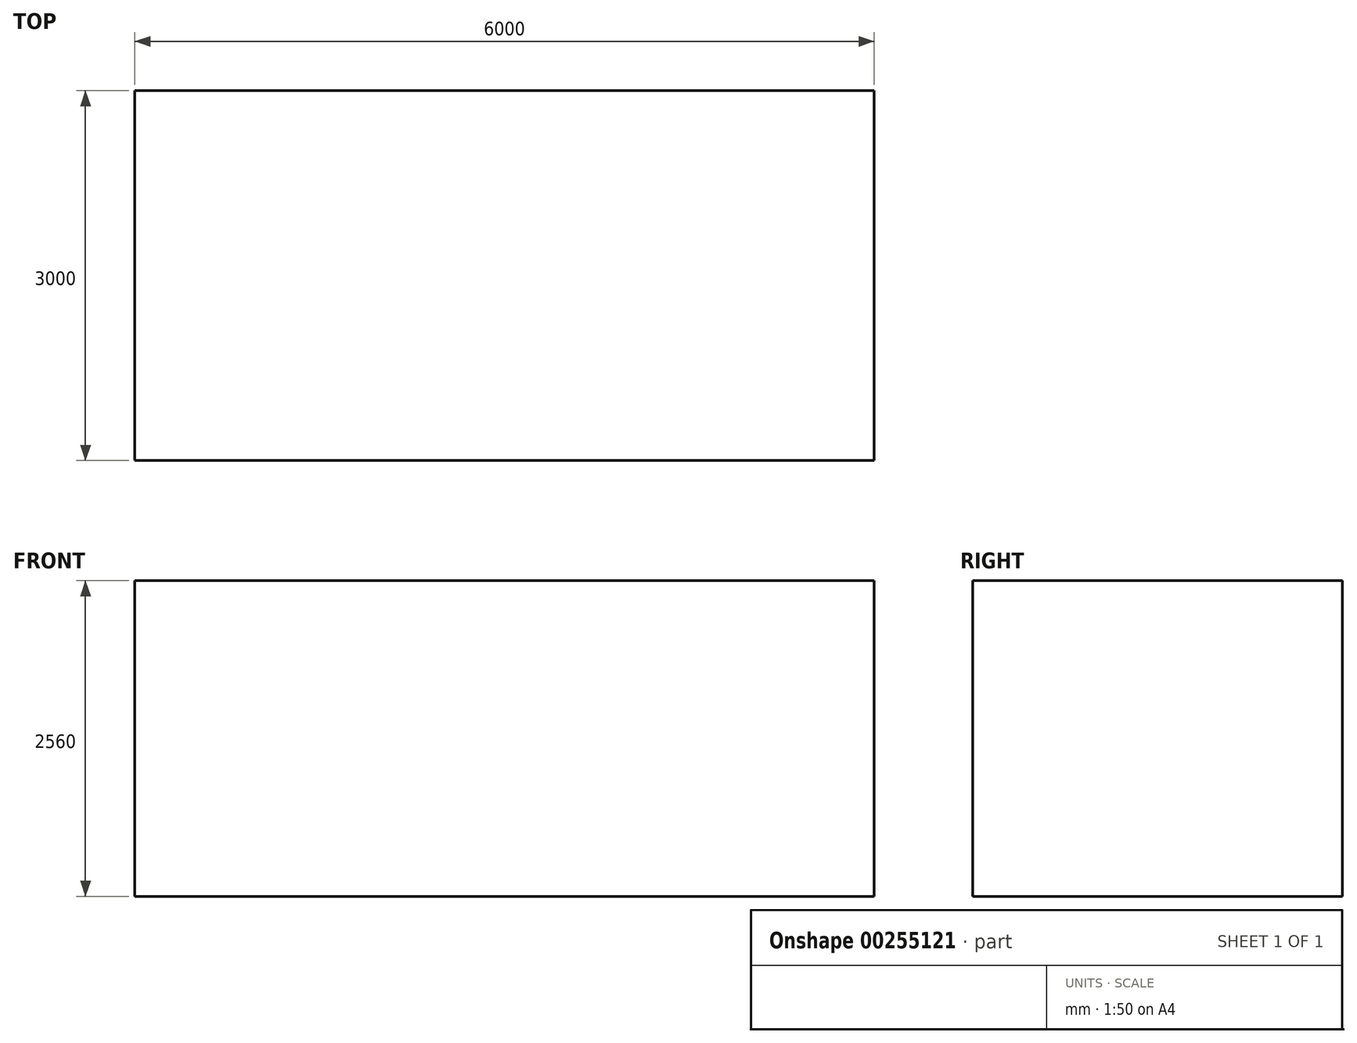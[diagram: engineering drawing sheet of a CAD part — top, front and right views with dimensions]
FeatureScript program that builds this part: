
annotation { "Feature Type Name" : "Feature", "Feature Type Description" : "" }
export const myFeature = defineFeature(function(context is Context, id is Id, definition is map)
    precondition{}
    {
        {
            var Q0;
            Q0=qCreatedBy(makeId("Top.planeOp"),FACE);
            var sketch = newSketch(context, id + "F0", { "sketchPlane" : qUnion([Q0])});
            skLineSegment(sketch, "E0.bottom", {"start": v(0, 0) * mm, "end": v(6000, 0) * mm});
            skLineSegment(sketch, "E0.top", {"start": v(0, -3000) * mm, "end": v(6000, -3000) * mm});
            skLineSegment(sketch, "E0.left", {"start": v(0, 0) * mm, "end": v(0, -3000) * mm});
            skLineSegment(sketch, "E0.right", {"start": v(6000, 0) * mm, "end": v(6000, -3000) * mm});
            skSolve(sketch);
        }
        {
            var Q0;
            Q0 = qSketchRegion(id + "F0", true);
            extrude(context, id + "F1", {"entities" : qUnion([Q0]), "depth" : 2560 * mm, "offsetDistance" : 25 * mm});
        }
    });
